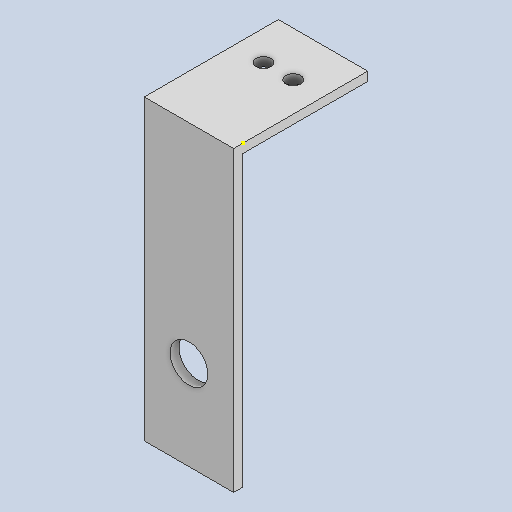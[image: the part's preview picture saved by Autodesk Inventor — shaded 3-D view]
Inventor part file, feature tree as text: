
AUTODESK INVENTOR PART (.ipt)
format: ipt  version: 2024 (Build 280153000, 153)  size: 261,120 bytes
history: native  units: mm
features: sketch x6, extrude x4
ambient origin geometry x8: Origin, YZ Plane, XZ Plane, XY Plane, X Axis, Y Axis, Z Axis, Center Point
bodies: Solid1 (feature_tree)
feature tree (10):
  extrude  "Extrusion1"  Depth=8.0mm
  extrude  "Extrusion2"  Depth=3.0mm TaperAngle=0.0deg
  extrude  "Extrusion3"  Depth=42.0mm TaperAngle=0.0deg
  extrude  "Extrusion4"  Depth=10.0mm
  sketch  "Sketch5"  dims[d10=5.0mm]
  sketch  "Sketch6"  dims[d11=15.0mm d12=5.0mm d13=10.0mm d14=42.0mm d15=0.0mm d16=12.7mm d17=30.0mm d18=15.0mm d19=42.0mm d20=0.0mm]
  sketch  "Sketch1"  dims[d0=30.0mm d1=8.0mm]
  sketch  "Sketch2"  dims[d2=100.0mm d3=3.0mm d4=0.0mm]
  sketch  "Sketch3"  dims[d5=3.0mm d6=42.0mm d7=0.0mm]
  sketch  "Sketch4"  dims[d8=15.0mm d9=10.0mm]
